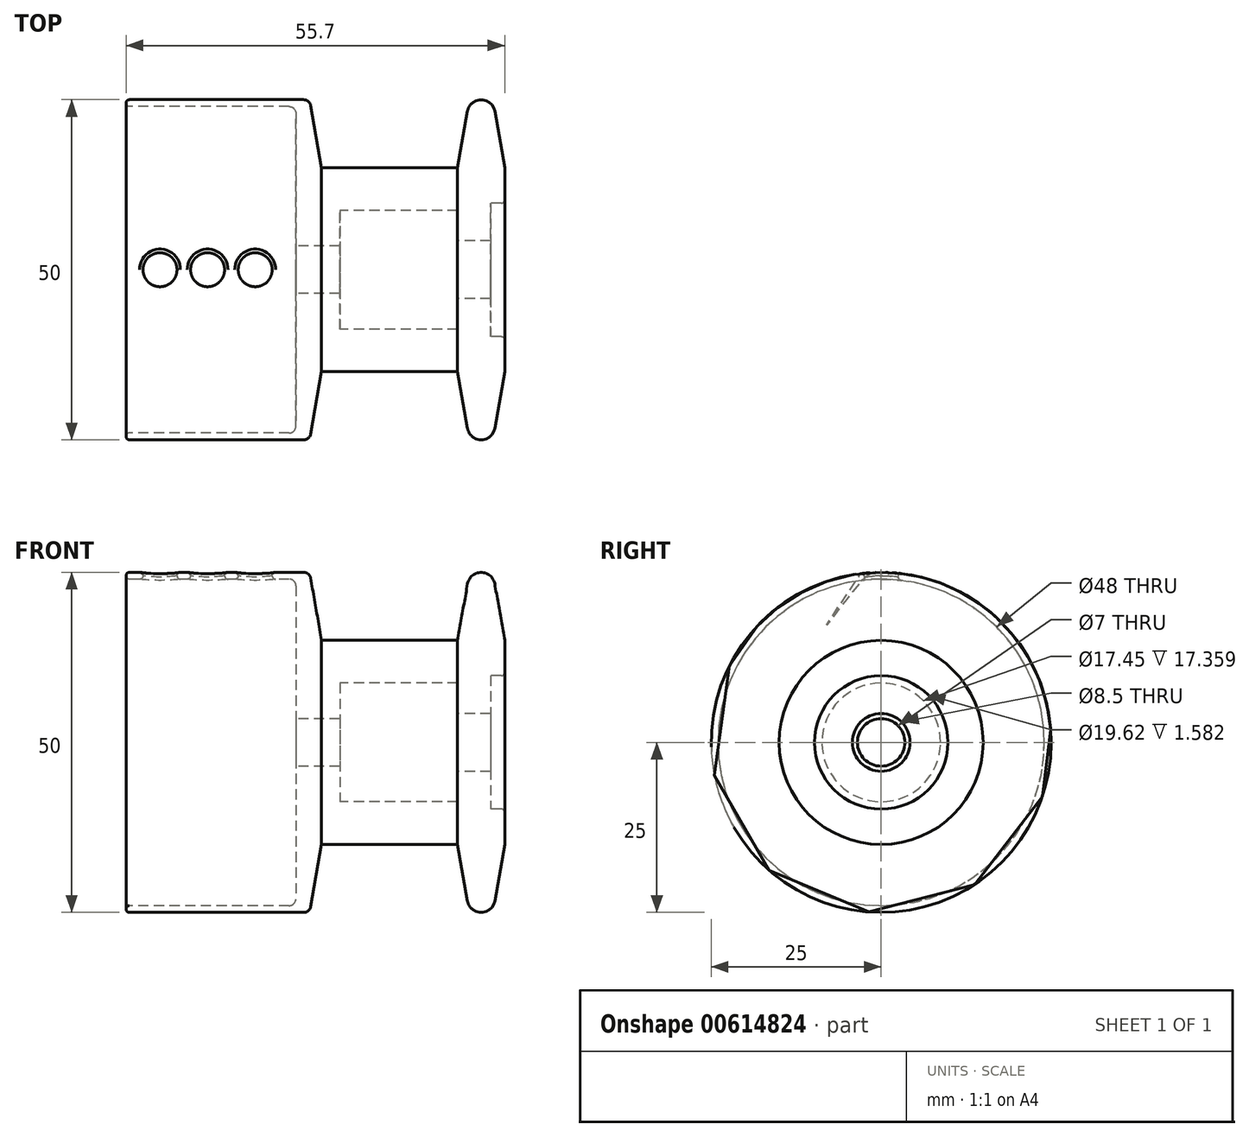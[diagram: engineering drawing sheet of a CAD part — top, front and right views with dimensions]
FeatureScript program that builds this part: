
annotation { "Feature Type Name" : "Feature", "Feature Type Description" : "" }
export const myFeature = defineFeature(function(context is Context, id is Id, definition is map)
    precondition{}
    {
        {
            var Q0;
            Q0=qCreatedBy(makeId("Front.planeOp"),FACE);
            var sketch = newSketch(context, id + "F0", { "sketchPlane" : qUnion([Q0])});
            skLineSegment(sketch, "E0", {"start": v(0, 25) * mm, "end": v(26.16, 25) * mm});
            skArc(sketch, "E1", {"start": v(54.23, 23.32) * mm, "mid": v(52.23, 25) * mm, "end": v(50.23, 23.32) * mm});
            skLineSegment(sketch, "E2", {"start": v(0, 25) * mm, "end": v(0, 24) * mm});
            skLineSegment(sketch, "E3", {"start": v(0, 24) * mm, "end": v(24, 24) * mm});
            skLineSegment(sketch, "E4", {"start": v(25, 23) * mm, "end": v(25, 3.5) * mm});
            skLineSegment(sketch, "E5", {"start": v(55.7, 15) * mm, "end": v(55.7, 9.8) * mm});
            skLineSegment(sketch, "E6", {"start": v(55.7, 9.8) * mm, "end": v(53.62, 9.8) * mm});
            skLineSegment(sketch, "E7", {"start": v(31.44, 8.72) * mm, "end": v(31.44, 3.5) * mm});
            skLineSegment(sketch, "E8", {"start": v(53.62, 9.8) * mm, "end": v(53.62, 4.25) * mm});
            skLineSegment(sketch, "E9", {"start": v(53.62, 4.25) * mm, "end": v(48.8, 4.25) * mm});
            skLineSegment(sketch, "E10", {"start": v(48.8, 4.25) * mm, "end": v(48.8, 8.72) * mm});
            skLineSegment(sketch, "E11", {"start": v(31.44, 8.72) * mm, "end": v(48.8, 8.72) * mm});
            skLineSegment(sketch, "E12", {"start": v(25, 3.5) * mm, "end": v(31.44, 3.5) * mm});
            skLineSegment(sketch, "E13", {"start": v(0, 0) * mm, "end": v(57.89, 0) * mm, "construction": true});
            skLineSegment(sketch, "E14", {"start": v(48.76, 15) * mm, "end": v(50.23, 23.32) * mm});
            skLineSegment(sketch, "E15", {"start": v(27.15, 24.17) * mm, "end": v(28.76, 15) * mm});
            skLineSegment(sketch, "E16", {"start": v(28.76, 15) * mm, "end": v(48.76, 15) * mm});
            skPoint(sketch, "E17", {"position": v(52.23, 25) * mm});
            skLineSegment(sketch, "E18", {"start": v(27, 25) * mm, "end": v(52.23, 25) * mm, "construction": true});
            skLineSegment(sketch, "E19", {"start": v(54.23, 23.32) * mm, "end": v(55.7, 15) * mm});
            skLineSegment(sketch, "E20", {"start": v(52.23, 25) * mm, "end": v(52.23, 12.44) * mm, "construction": true});
            skPoint(sketch, "E21.visualSharp", {"position": v(27, 25) * mm});
            skArc(sketch, "E21.filletArc", {"start": v(27.15, 24.17) * mm, "mid": v(26.8, 24.77) * mm, "end": v(26.16, 25) * mm});
            skPoint(sketch, "E22.visualSharp", {"position": v(25, 24) * mm});
            skArc(sketch, "E22.filletArc", {"start": v(25, 23) * mm, "mid": v(24.7, 23.7) * mm, "end": v(24, 24) * mm});
            skSolve(sketch);
        }
        {
            var Q0;
            Q0=makeQuery(id+"F0.imprint","IMPRINT",FACE,{"disambiguationData":[TD([[makeQuery(id+"F0.imprint","IMPRINT",EDGE,{"derivedFrom":sQuery(id+"F0.wireOp",EDGE,"E0")}),-1.0]])]});
            var Q1;
            Q1=sQuery(id+"F0.wireOp",EDGE,"E13");
            revolve(context, id + "F1", {"entities" : qUnion([Q0]), "axis" : qUnion([Q1]), "revolveType" : RevolveType.FULL});
        }
        {
            var Q0;
            Q0=qCreatedBy(makeId("Top.planeOp"),FACE);
            var sketch = newSketch(context, id + "F2", { "sketchPlane" : qUnion([Q0])});
            skLineSegment(sketch, "E23.0", {"start": v(26.16, -25) * mm, "end": v(26.16, 25) * mm});
            skLineSegment(sketch, "E24", {"start": v(0, 25) * mm, "end": v(26.16, 25) * mm});
            skLineSegment(sketch, "E25", {"start": v(26.16, -25) * mm, "end": v(0, -25) * mm});
            skPoint(sketch, "E26.0", {"position": v(24, 0) * mm});
            skCircle(sketch, "E27", {"center": v(5, 0) * mm, "radius": 2.5 * mm});
            skCircle(sketch, "E28", {"center": v(12, 0) * mm, "radius": 2.5 * mm});
            skCircle(sketch, "E29", {"center": v(19, 0) * mm, "radius": 2.5 * mm});
            skLineSegment(sketch, "E30", {"start": v(5, 0) * mm, "end": v(12, 0) * mm, "construction": true});
            skLineSegment(sketch, "E31", {"start": v(19, 0) * mm, "end": v(24, 0) * mm, "construction": true});
            skLineSegment(sketch, "E32", {"start": v(12, 0) * mm, "end": v(19, 0) * mm, "construction": true});
            skLineSegment(sketch, "E33", {"start": v(0, 0) * mm, "end": v(5, 0) * mm, "construction": true});
            skSolve(sketch);
        }
        {
            var Q0;
            Q0 = qSketchRegion(id + "F2", true);
            extrude(context, id + "F3", {"entities" : qUnion([Q0]), "operationType" : NewBodyOperationType.REMOVE, "endBound" : BoundingType.THROUGH_ALL, "depth" : 25 * mm, "offsetDistance" : 25 * mm});
        }
        {
            var Q0;
            Q0=makeQuery(id+"F3.boolean.opBoolean","INTERSECT",EDGE,{"derivedFrom":[makeQuery(id+"F1.opRevolve","SWEPT_FACE",FACE,{"disambiguationData":[OSD([sQuery(id+"F0.wireOp",EDGE,"E0")])]}),makeQuery(id+"F3.opExtrude","SWEPT_FACE",FACE,{"disambiguationData":[OSD([sQuery(id+"F2.wireOp",EDGE,"E29")])]})]});
            var Q1;
            Q1=makeQuery(id+"F3.boolean.opBoolean","INTERSECT",EDGE,{"derivedFrom":[makeQuery(id+"F1.opRevolve","SWEPT_FACE",FACE,{"disambiguationData":[OSD([sQuery(id+"F0.wireOp",EDGE,"E0")])]}),makeQuery(id+"F3.opExtrude","SWEPT_FACE",FACE,{"disambiguationData":[OSD([sQuery(id+"F2.wireOp",EDGE,"E28")])]})]});
            var Q2;
            Q2=makeQuery(id+"F3.boolean.opBoolean","INTERSECT",EDGE,{"derivedFrom":[makeQuery(id+"F1.opRevolve","SWEPT_FACE",FACE,{"disambiguationData":[OSD([sQuery(id+"F0.wireOp",EDGE,"E0")])]}),makeQuery(id+"F3.opExtrude","SWEPT_FACE",FACE,{"disambiguationData":[OSD([sQuery(id+"F2.wireOp",EDGE,"E27")])]})]});
            var Q3;
            Q3=makeQuery(id+"F3.boolean.opBoolean","INTERSECT",EDGE,{"derivedFrom":[makeQuery(id+"F1.opRevolve","SWEPT_FACE",FACE,{"disambiguationData":[OSD([sQuery(id+"F0.wireOp",EDGE,"E3")])]}),makeQuery(id+"F3.opExtrude","SWEPT_FACE",FACE,{"disambiguationData":[OSD([sQuery(id+"F2.wireOp",EDGE,"E29")])]})]});
            var Q4;
            Q4=makeQuery(id+"F3.boolean.opBoolean","INTERSECT",EDGE,{"derivedFrom":[makeQuery(id+"F1.opRevolve","SWEPT_FACE",FACE,{"disambiguationData":[OSD([sQuery(id+"F0.wireOp",EDGE,"E3")])]}),makeQuery(id+"F3.opExtrude","SWEPT_FACE",FACE,{"disambiguationData":[OSD([sQuery(id+"F2.wireOp",EDGE,"E28")])]})]});
            var Q5;
            Q5=makeQuery(id+"F3.boolean.opBoolean","INTERSECT",EDGE,{"derivedFrom":[makeQuery(id+"F1.opRevolve","SWEPT_FACE",FACE,{"disambiguationData":[OSD([sQuery(id+"F0.wireOp",EDGE,"E3")])]}),makeQuery(id+"F3.opExtrude","SWEPT_FACE",FACE,{"disambiguationData":[OSD([sQuery(id+"F2.wireOp",EDGE,"E27")])]})]});
            fillet(context, id + "F4", {"entities" : qUnion([Q0, Q1, Q2, Q3, Q4, Q5]), "radius" : 0.5 * mm, "tangentPropagation" : true, "allowEdgeOverflow" : false});
        }
        {
            var Q0;
            Q0=makeQuery(id+"F1.opRevolve","SWEPT_EDGE",EDGE,{"disambiguationData":[OSD([sQuery(id+"F0.wireOp",EDGE,"E0"),sQuery(id+"F0.wireOp",EDGE,"E2")])]});
            var Q1;
            Q1=makeQuery(id+"F1.opRevolve","SWEPT_EDGE",EDGE,{"disambiguationData":[OSD([sQuery(id+"F0.wireOp",EDGE,"E2"),sQuery(id+"F0.wireOp",EDGE,"E3")])]});
            var Q2;
            Q2=makeQuery(id+"F1.opRevolve","SWEPT_EDGE",EDGE,{"disambiguationData":[OSD([sQuery(id+"F0.wireOp",EDGE,"E5"),sQuery(id+"F0.wireOp",EDGE,"E6")])]});
            fillet(context, id + "F5", {"entities" : qUnion([Q0, Q1, Q2]), "radius" : 0.5 * mm, "tangentPropagation" : true, "allowEdgeOverflow" : false});
        }
    });
